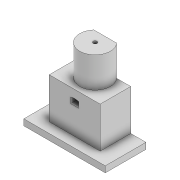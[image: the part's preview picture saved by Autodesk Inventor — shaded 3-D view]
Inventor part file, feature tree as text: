
AUTODESK INVENTOR PART (.ipt)
format: ipt  version: 2022 (Build 260153000, 153)  size: 166,912 bytes
history: native  units: mm
features: extrude x9, sketch x9, projected_geometry x2
ambient origin geometry x8: Origin, YZ Plane, XZ Plane, XY Plane, X Axis, Y Axis, Z Axis, Center Point
bodies: Solid1 (feature_tree)
feature tree (20):
  extrude  "Extrusion1"  Depth=25.0mm
  extrude  "Extrusion2"  Depth=20.0mm TaperAngle=0.0deg
  extrude  "Extrusion3"  Depth=100.0mm TaperAngle=0.0deg
  extrude  "Extrusion4"  Depth=15.0mm TaperAngle=0.0deg
  extrude  "Extrusion6"  Depth=40.0mm
  extrude  "Extrusion8"  Depth=10.0mm TaperAngle=0.0deg
  extrude  "Extrusion9"  Depth=2.0mm
  extrude  "Extrusion10"  Depth=3.0mm
  extrude  "Extrusion11"  Depth=15.0mm
  sketch  "Sketch1"  dims[d0=12.2mm d1=25.0mm]
  sketch  "Sketch2"  dims[d2=20.0mm d3=20.0mm d4=0.0mm]
  sketch  "Sketch3"  dims[d5=1.9mm d6=100.0mm d7=0.0mm]
  projected_geometry  "Projected Loop1"
  sketch  "Sketch4"  dims[d8=15.0mm d9=15.0mm d10=0.0mm]
  sketch  "Sketch6"  dims[d11=30.0mm d12=40.0mm]
  sketch  "Sketch8"  dims[d13=3.0mm d14=0.0mm d21=10.0mm d22=0.0mm]
  sketch  "Sketch9"  dims[d26=100.0mm d27=0.0mm d28=2.0mm]
  projected_geometry  "Projected Loop3"
  sketch  "Sketch10"  dims[d29=2.0mm d30=3.0mm]
  sketch  "Sketch11"  dims[d31=5.0mm d32=0.0mm d33=9.8mm d34=15.0mm d35=0.0mm d36=100.0mm d37=0.0mm]
